# Revit family: VL2S-GP150xSWxxxWx
name_source: partatom
category: Leuchten
units: mm (PartAtom-declared; Revit-internal decimal feet)

## family parameters
Basisbauteil = Fläche
Beim Laden mit Abzugskörper schneiden = Nein
Bemaßung runder Anschluss = Durchmesser verwenden
Gemeinsam genutzt = Nein
Lichtquelle = Ja
OmniClass-Nummer = 23.80.70.11
OmniClass-Titel = Luminaries for Internal Lighting
Raumberechnungspunkt = Nein
Teiletyp = Normal

## types (8) — shared parameters
Baugruppenkennzeichen = D5020200
Datei für fotometrisches Netz = VLGFP1501-5NDWS840W0800.IES
Emissionsform beim Rendern sichtbar = Nein
Farbfilter = 16777215
Farbtemperaturverschiebung bei Dämpfen der Lampe = <Keine Auswahl>
Hersteller = RIDI Leuchten GmbH
Lampe = LED
Neigungswinkel = 90.00°
URL = www.ridi.de
Von Breite des Rechtecks ausssenden = 1477 mm  [stored 4.8458 ft]
Von Länge des Rechtecks aussenden = 64 mm  [stored 0.209974 ft]
brand = RIDI
conformity mark = CE
electrical safety class = 1
height = 86 mm  [stored 0.282152 ft]
ingress protection (IP) code = IP40
length = 1500 mm  [stored 4.92126 ft]
nominal frequency = 50-60Hz
nominal voltage = 230
voltage type (AC, DC, UC) = AC
weight = 2,2 kg
width = 67 mm
zero-valued in all types: Vorgabe-Ansicht

## per-type parameters (varying)
| type | Modell | Scheinlast | product name | rated input power |
| VL2S-GP150-5FLSW840W0850 | 2550117SW | 58 VA | VL2S-GP150-5FLSW840W0850 | 58 |
| VL2S-GP150-5FLSW830W0850 | 2550119SW | 58 VA | VL2S-GP150-5FLSW830W0850 | 58 |
| VL2S-GP150-5FLSW850W0850 | 2550120SW | 58 VA | VL2S-GP150-5FLSW850W0850 | 58 |
| VL2S-GP150-5FLSW865W0850 | 2550121SW | 58 VA | VL2S-GP150-5FLSW865W0850 | 58 |
| VL2S-GP150-7DASW840W0850 | 2560118SW | 55 VA | VL2S-GP150-7DASW840W0850 | 55 |
| VL2S-GP150-7DASW830W0800 | 2560122SW | 55 VA | VL2S-GP150-7DASW830W0800 | 55 |
| VL2S-GP150-7DASW850W0850 | 2560123SW | 55 VA | VL2S-GP150-7DASW850W0850 | 55 |
| VL2S-GP150-7DASW865W0800 | 2560124SW | 55 VA | VL2S-GP150-7DASW850W0850 | 55 |

note: [stored X ft] marks values corroborated as IEEE doubles in the binary element streams (Revit-internal decimal feet)
